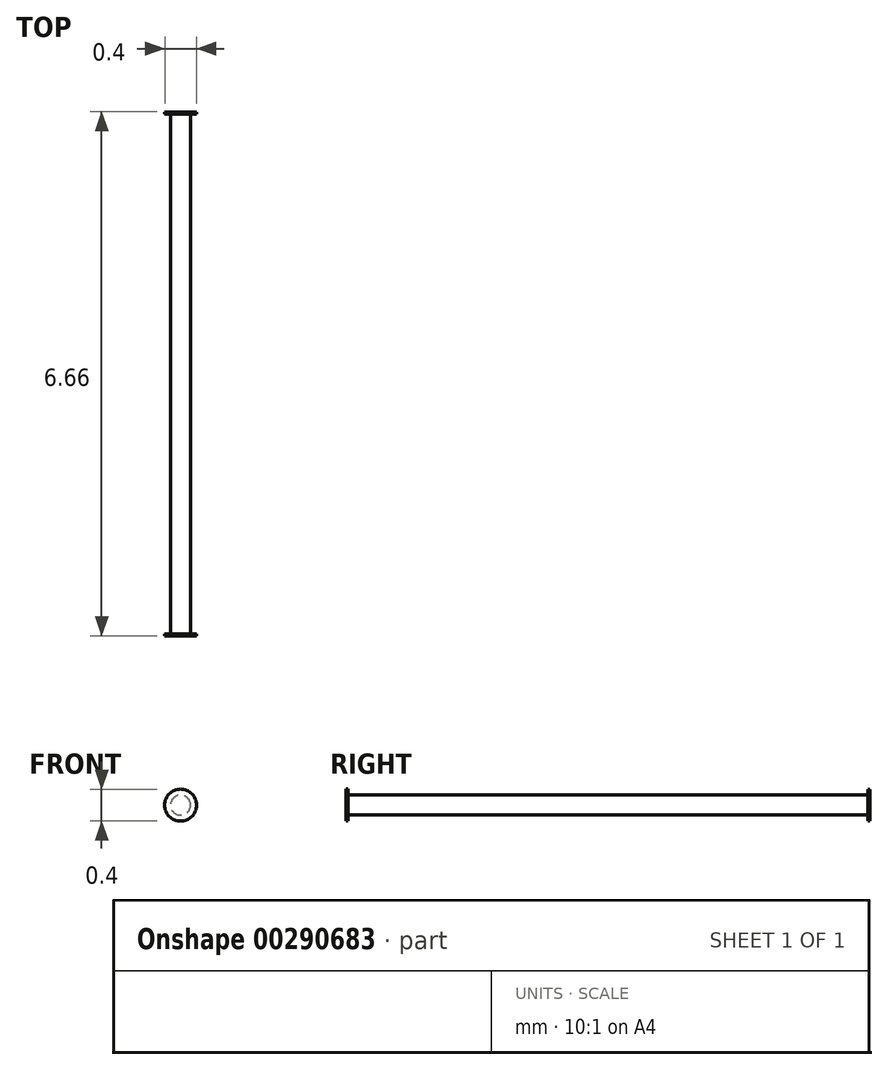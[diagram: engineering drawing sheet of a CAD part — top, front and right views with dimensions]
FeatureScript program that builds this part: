
annotation { "Feature Type Name" : "Feature", "Feature Type Description" : "" }
export const myFeature = defineFeature(function(context is Context, id is Id, definition is map)
    precondition{}
    {
        {
            var Q0;
            Q0=qCreatedBy(makeId("Front.planeOp"),FACE);
            var sketch = newSketch(context, id + "F0", { "sketchPlane" : qUnion([Q0])});
            skCircle(sketch, "E0", {"center": v(0, 0) * mm, "radius": 0.13 * mm});
            skSolve(sketch);
        }
        {
            var Q0;
            Q0=makeQuery(id+"F0.imprint","IMPRINT",FACE,{"disambiguationData":[TD([[makeQuery(id+"F0.imprint","IMPRINT",EDGE,{"derivedFrom":sQuery(id+"F0.wireOp",EDGE,"E0")}),1.0]])]});
            extrude(context, id + "F1", {"entities" : qUnion([Q0]), "depth" : 6.6 * mm});
        }
        {
            var Q0;
            Q0=makeQuery(id+"F1.opExtrude","CAP_FACE",FACE,{"disambiguationData":[OSD([sQuery(id+"F0.wireOp",EDGE,"E0")])],"isStart":false});
            var sketch = newSketch(context, id + "F2", { "sketchPlane" : qUnion([Q0])});
            skCircle(sketch, "E1", {"center": v(0, 0) * mm, "radius": 0.2 * mm});
            skSolve(sketch);
        }
        {
            var Q0;
            Q0=makeQuery(id+"F2.imprint","IMPRINT",FACE,{"disambiguationData":[TD([[makeQuery(id+"F2.imprint","IMPRINT",EDGE,{"derivedFrom":sQuery(id+"F2.wireOp",EDGE,"E1")}),1.0]])]});
            var Q1;
            Q1=makeQuery(id+"F2.imprint","IMPRINT",FACE,{"disambiguationData":[TD([[makeQuery(id+"F2.imprint","IMPRINT",EDGE,{"derivedFrom":makeQuery(id+"F1.opExtrude","CAP_EDGE",EDGE,{"disambiguationData":[OSD([sQuery(id+"F0.wireOp",EDGE,"E0")])],"isStart":false})}),1.0]])]});
            extrude(context, id + "F3", {"entities" : qUnion([Q0, Q1]), "operationType" : NewBodyOperationType.ADD, "depth" : 0.03 * mm});
        }
        {
            var Q0;
            Q0=makeQuery(id+"F1.opExtrude","CAP_FACE",FACE,{"disambiguationData":[OSD([sQuery(id+"F0.wireOp",EDGE,"E0")])],"isStart":true});
            var sketch = newSketch(context, id + "F4", { "sketchPlane" : qUnion([Q0])});
            skCircle(sketch, "E2", {"center": v(0, 0) * mm, "radius": 0.2 * mm});
            skSolve(sketch);
        }
        {
            var Q0;
            Q0=makeQuery(id+"F4.imprint","IMPRINT",FACE,{"disambiguationData":[TD([[makeQuery(id+"F4.imprint","IMPRINT",EDGE,{"derivedFrom":sQuery(id+"F4.wireOp",EDGE,"E2")}),1.0]])]});
            var Q1;
            Q1=makeQuery(id+"F4.imprint","IMPRINT",FACE,{"disambiguationData":[TD([[makeQuery(id+"F4.imprint","IMPRINT",EDGE,{"derivedFrom":makeQuery(id+"F1.opExtrude","CAP_EDGE",EDGE,{"disambiguationData":[OSD([sQuery(id+"F0.wireOp",EDGE,"E0")])],"isStart":true})}),-1.0]])]});
            extrude(context, id + "F5", {"entities" : qUnion([Q0, Q1]), "operationType" : NewBodyOperationType.ADD, "depth" : 0.03 * mm});
        }
    });
